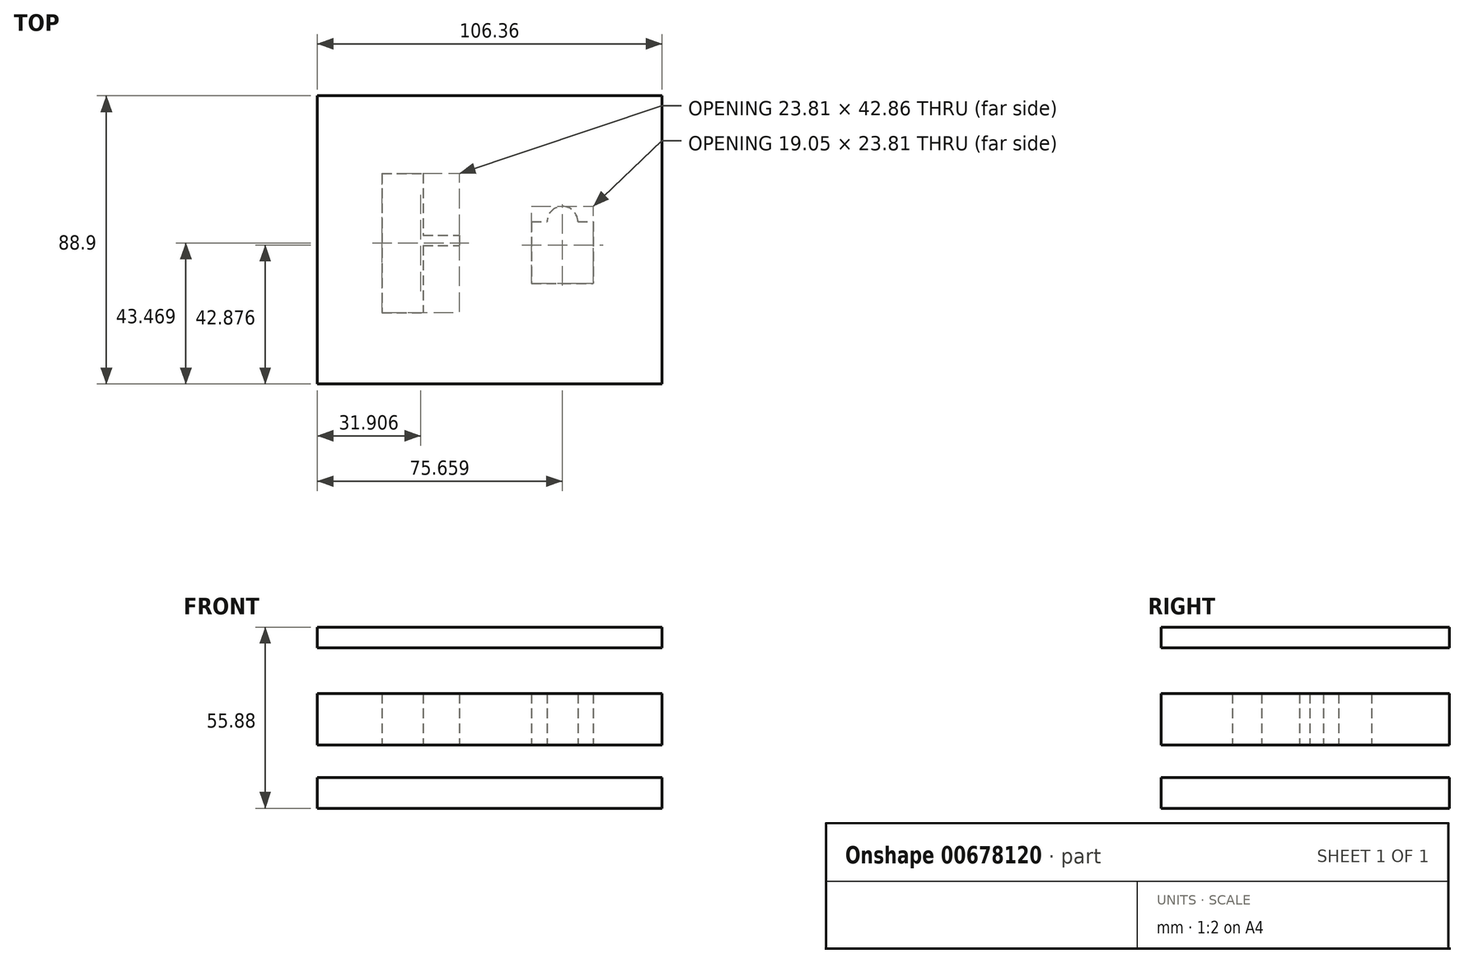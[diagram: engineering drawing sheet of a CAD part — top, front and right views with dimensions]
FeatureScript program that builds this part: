
annotation { "Feature Type Name" : "Feature", "Feature Type Description" : "" }
export const myFeature = defineFeature(function(context is Context, id is Id, definition is map)
    precondition{}
    {
        {
            var Q0;
            Q0=qCreatedBy(makeId("Top.planeOp"),FACE);
            var sketch = newSketch(context, id + "F0", { "sketchPlane" : qUnion([Q0])});
            skLineSegment(sketch, "E0.bottom", {"start": v(0, 88.9) * mm, "end": v(106.36, 88.9) * mm});
            skLineSegment(sketch, "E0.top", {"start": v(0, 0) * mm, "end": v(106.36, 0) * mm});
            skLineSegment(sketch, "E0.left", {"start": v(0, 88.9) * mm, "end": v(0, 0) * mm});
            skLineSegment(sketch, "E0.right", {"start": v(106.36, 88.9) * mm, "end": v(106.36, 0) * mm});
            skSolve(sketch);
        }
        {
            var Q0;
            Q0=makeQuery(id+"F0.imprint","IMPRINT",FACE,{"disambiguationData":[TD([[makeQuery(id+"F0.imprint","IMPRINT",EDGE,{"derivedFrom":sQuery(id+"F0.wireOp",EDGE,"E0.bottom")}),-1.0]])]});
            extrude(context, id + "F1", {"entities" : qUnion([Q0]), "depth" : 9.52 * mm, "offsetDistance" : 25 * mm});
        }
        {
            var Q0;
            Q0=makeQuery(id+"F1.opExtrude","CAP_FACE",FACE,{"disambiguationData":[OSD([sQuery(id+"F0.wireOp",EDGE,"E0.bottom"),sQuery(id+"F0.wireOp",EDGE,"E0.top"),sQuery(id+"F0.wireOp",EDGE,"E0.left"),sQuery(id+"F0.wireOp",EDGE,"E0.right")])],"isStart":false});
            cPlane(context, id + "F2", {"entities" : qUnion([Q0]), "cplaneType" : CPlaneType.OFFSET, "offset" : 10 * mm, "width" : 150 * mm, "height" : 150 * mm});
        }
        {
            var Q0;
            Q0=qCreatedBy(id+"F2.planeOp",FACE);
            var sketch = newSketch(context, id + "F3", { "sketchPlane" : qUnion([Q0])});
            skLineSegment(sketch, "E1.bottom", {"start": v(0, 88.9) * mm, "end": v(106.36, 88.9) * mm});
            skLineSegment(sketch, "E1.top", {"start": v(0, 0) * mm, "end": v(106.36, 0) * mm});
            skLineSegment(sketch, "E1.left", {"start": v(0, 88.9) * mm, "end": v(0, 0) * mm});
            skLineSegment(sketch, "E1.right", {"start": v(106.36, 88.9) * mm, "end": v(106.36, 0) * mm});
            skLineSegment(sketch, "E2.bottom", {"start": v(20, 64.9) * mm, "end": v(32.7, 64.9) * mm});
            skLineSegment(sketch, "E2.top", {"start": v(20, 22.04) * mm, "end": v(32.7, 22.04) * mm});
            skLineSegment(sketch, "E2.left", {"start": v(20, 64.9) * mm, "end": v(20, 22.04) * mm});
            skLineSegment(sketch, "E2.right", {"start": v(32.7, 64.9) * mm, "end": v(32.7, 22.04) * mm});
            skLineSegment(sketch, "E3.bottom", {"start": v(32.7, 42.67) * mm, "end": v(43.81, 42.67) * mm});
            skLineSegment(sketch, "E3.top", {"start": v(32.7, 45.85) * mm, "end": v(43.81, 45.85) * mm});
            skLineSegment(sketch, "E3.left", {"start": v(32.7, 45.85) * mm, "end": v(32.7, 42.67) * mm});
            skLineSegment(sketch, "E3.right", {"start": v(43.81, 45.85) * mm, "end": v(43.81, 42.67) * mm});
            skLineSegment(sketch, "E4.bottom", {"start": v(66.13, 50.02) * mm, "end": v(85.18, 50.02) * mm});
            skLineSegment(sketch, "E4.top", {"start": v(66.13, 30.97) * mm, "end": v(85.18, 30.97) * mm});
            skLineSegment(sketch, "E4.left", {"start": v(66.13, 50.02) * mm, "end": v(66.13, 30.97) * mm});
            skLineSegment(sketch, "E4.right", {"start": v(85.18, 50.02) * mm, "end": v(85.18, 30.97) * mm});
            skCircle(sketch, "E5", {"center": v(75.66, 50.02) * mm, "radius": 4.76 * mm});
            skSolve(sketch);
        }
        {
            var Q0;
            Q0=makeQuery(id+"F3.imprint","IMPRINT",FACE,{"disambiguationData":[TD([[makeQuery(id+"F3.imprint","IMPRINT",EDGE,{"derivedFrom":sQuery(id+"F3.wireOp",EDGE,"E1.bottom")}),-1.0]])]});
            extrude(context, id + "F4", {"entities" : qUnion([Q0]), "depth" : 15.88 * mm, "offsetDistance" : 25 * mm});
        }
        {
            var Q0;
            Q0=makeQuery(id+"F1.opExtrude","CAP_FACE",FACE,{"disambiguationData":[OSD([sQuery(id+"F0.wireOp",EDGE,"E0.bottom"),sQuery(id+"F0.wireOp",EDGE,"E0.top"),sQuery(id+"F0.wireOp",EDGE,"E0.left"),sQuery(id+"F0.wireOp",EDGE,"E0.right")])],"isStart":false});
            cPlane(context, id + "F5", {"entities" : qUnion([Q0]), "cplaneType" : CPlaneType.OFFSET, "offset" : 40 * mm, "width" : 150 * mm, "height" : 150 * mm});
        }
        {
            var Q0;
            Q0=qCreatedBy(id+"F5.planeOp",FACE);
            var sketch = newSketch(context, id + "F6", { "sketchPlane" : qUnion([Q0])});
            skLineSegment(sketch, "E6.bottom", {"start": v(0, 88.9) * mm, "end": v(106.36, 88.9) * mm});
            skLineSegment(sketch, "E6.top", {"start": v(0, 0) * mm, "end": v(106.36, 0) * mm});
            skLineSegment(sketch, "E6.left", {"start": v(0, 88.9) * mm, "end": v(0, 0) * mm});
            skLineSegment(sketch, "E6.right", {"start": v(106.36, 88.9) * mm, "end": v(106.36, 0) * mm});
            skSolve(sketch);
        }
        {
            var Q0;
            Q0=makeQuery(id+"F6.imprint","IMPRINT",FACE,{"disambiguationData":[TD([[makeQuery(id+"F6.imprint","IMPRINT",EDGE,{"derivedFrom":sQuery(id+"F6.wireOp",EDGE,"E6.bottom")}),-1.0]])]});
            extrude(context, id + "F7", {"entities" : qUnion([Q0]), "depth" : 6.35 * mm, "offsetDistance" : 25 * mm});
        }
    });
